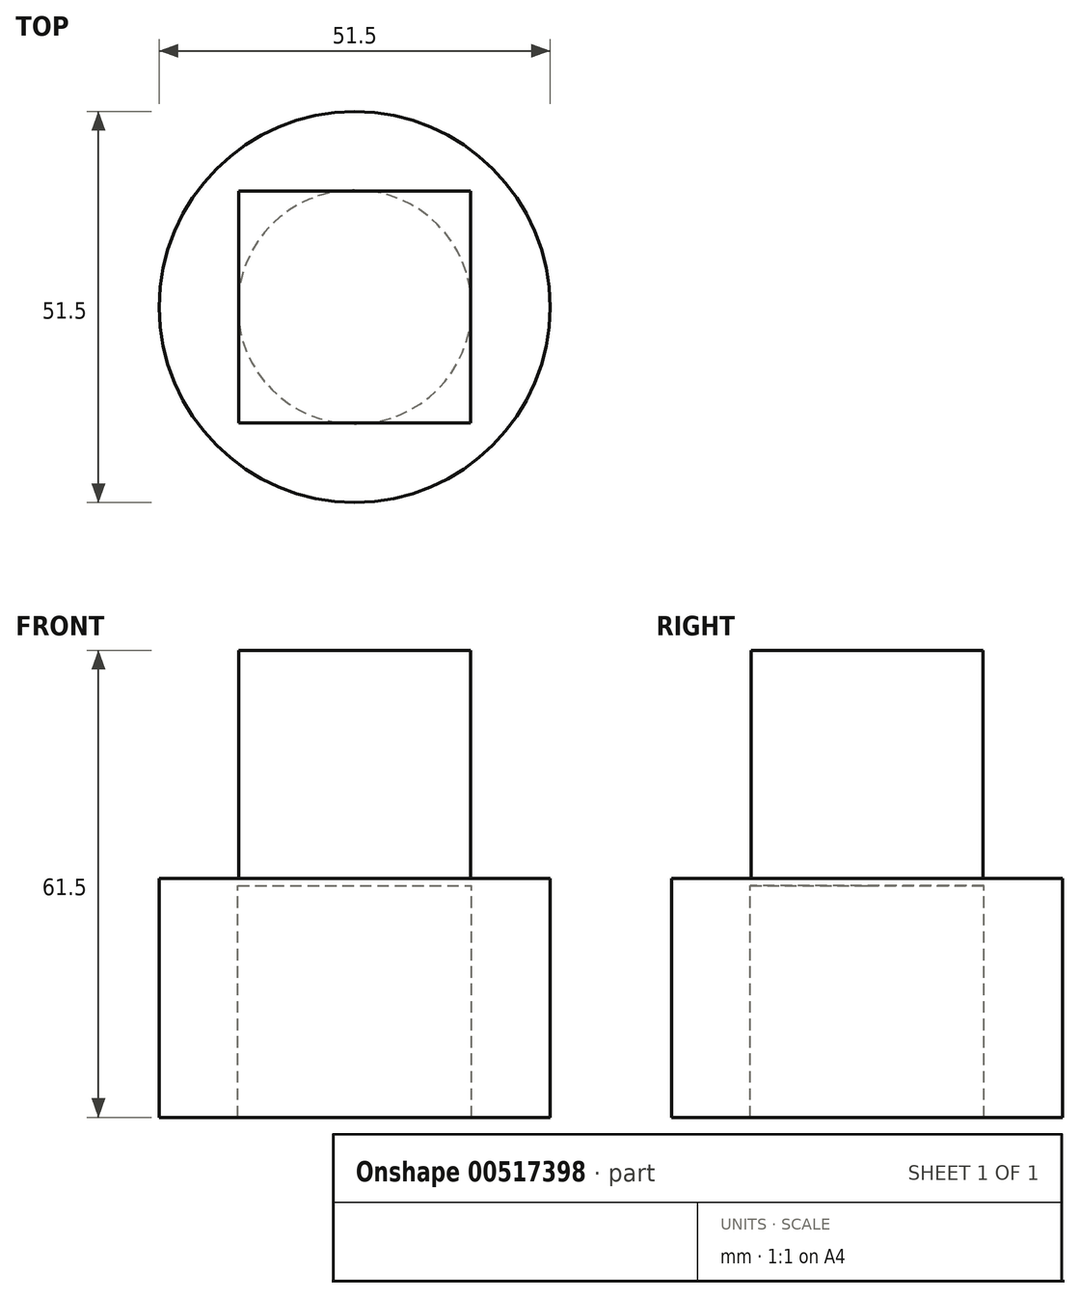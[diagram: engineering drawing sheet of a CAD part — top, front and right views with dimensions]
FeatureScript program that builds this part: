
annotation { "Feature Type Name" : "Feature", "Feature Type Description" : "" }
export const myFeature = defineFeature(function(context is Context, id is Id, definition is map)
    precondition{}
    {
        {
            var Q0;
            Q0=qCreatedBy(makeId("Top.planeOp"),FACE);
            var sketch = newSketch(context, id + "F0", { "sketchPlane" : qUnion([Q0])});
            skLineSegment(sketch, "E0.bottom", {"start": v(15.25, 15.25) * mm, "end": v(-15.25, 15.25) * mm});
            skLineSegment(sketch, "E0.top", {"start": v(15.25, -15.25) * mm, "end": v(-15.25, -15.25) * mm});
            skLineSegment(sketch, "E0.left", {"start": v(15.25, 15.25) * mm, "end": v(15.25, -15.25) * mm});
            skLineSegment(sketch, "E0.right", {"start": v(-15.25, 15.25) * mm, "end": v(-15.25, -15.25) * mm});
            skPoint(sketch, "E0.middle", {"position": v(0, 0) * mm});
            skSolve(sketch);
        }
        {
            var Q0;
            Q0=makeQuery(id+"F0.imprint","IMPRINT",FACE,{"disambiguationData":[TD([[makeQuery(id+"F0.imprint","IMPRINT",EDGE,{"derivedFrom":sQuery(id+"F0.wireOp",EDGE,"E0.bottom")}),1.0]])]});
            extrude(context, id + "F1", {"entities" : qUnion([Q0]), "depth" : 30 * mm, "offsetDistance" : 25 * mm});
        }
        {
            var Q0;
            Q0=makeQuery(id+"F1.opExtrude","CAP_FACE",FACE,{"disambiguationData":[OSD([sQuery(id+"F0.wireOp",EDGE,"E0.bottom"),sQuery(id+"F0.wireOp",EDGE,"E0.top"),sQuery(id+"F0.wireOp",EDGE,"E0.left"),sQuery(id+"F0.wireOp",EDGE,"E0.right")])],"isStart":true});
            var sketch = newSketch(context, id + "F2", { "sketchPlane" : qUnion([Q0])});
            skCircle(sketch, "E1", {"center": v(0, 0) * mm, "radius": 25.75 * mm});
            skCircle(sketch, "E2", {"center": v(0, 0) * mm, "radius": 15 * mm});
            skSolve(sketch);
        }
        {
            var Q0;
            Q0=makeQuery(id+"F2.imprint","IMPRINT",FACE,{"disambiguationData":[TD([[makeQuery(id+"F2.imprint","IMPRINT",EDGE,{"derivedFrom":sQuery(id+"F2.wireOp",EDGE,"E1")}),1.0]])]});
            var Q1;
            {var subQ0=sQuery(id+"F2.wireOp",EDGE,"E2");var subQ1=makeQuery(id+"F2.imprint","INTERSECT",VERTEX,{"derivedFrom":[makeQuery(id+"F1.opExtrude","CAP_EDGE",EDGE,{"disambiguationData":[OSD([sQuery(id+"F0.wireOp",EDGE,"E0.top")])],"isStart":true}),subQ0]});Q1=makeQuery(id+"F2.imprint","IMPRINT",FACE,{"disambiguationData":[TD([[makeQuery(id+"F2.imprint","IMPRINT",EDGE,{"disambiguationData":[TD([[subQ1,1.0]])],"derivedFrom":subQ0}),1.0]])]});}
            var Q2;
            {var subQ0=sQuery(id+"F2.wireOp",EDGE,"E2");var subQ1=makeQuery(id+"F1.opExtrude","CAP_EDGE",EDGE,{"disambiguationData":[OSD([sQuery(id+"F0.wireOp",EDGE,"E0.top")])],"isStart":true});var subQ2=makeQuery(id+"F2.imprint","INTERSECT",VERTEX,{"derivedFrom":[subQ1,subQ0]});Q2=makeQuery(id+"F2.imprint","IMPRINT",FACE,{"disambiguationData":[TD([[makeQuery(id+"F2.imprint","IMPRINT",EDGE,{"disambiguationData":[TD([[subQ2,-1.0]])],"derivedFrom":subQ0}),-1.0]])]});}
            var Q3;
            {var subQ0=sQuery(id+"F2.wireOp",EDGE,"E2");var subQ1=makeQuery(id+"F1.opExtrude","CAP_EDGE",EDGE,{"disambiguationData":[OSD([sQuery(id+"F0.wireOp",EDGE,"E0.top")])],"isStart":true});var subQ2=makeQuery(id+"F2.imprint","INTERSECT",VERTEX,{"derivedFrom":[subQ1,subQ0]});Q3=makeQuery(id+"F2.imprint","IMPRINT",FACE,{"disambiguationData":[TD([[makeQuery(id+"F2.imprint","IMPRINT",EDGE,{"disambiguationData":[TD([[subQ2,1.0]])],"derivedFrom":subQ0}),-1.0]])]});}
            var Q4;
            {var subQ0=sQuery(id+"F2.wireOp",EDGE,"E2");var subQ1=makeQuery(id+"F1.opExtrude","CAP_EDGE",EDGE,{"disambiguationData":[OSD([sQuery(id+"F0.wireOp",EDGE,"E0.left")])],"isStart":true});var subQ2=makeQuery(id+"F2.imprint","INTERSECT",VERTEX,{"derivedFrom":[subQ1,subQ0]});Q4=makeQuery(id+"F2.imprint","IMPRINT",FACE,{"disambiguationData":[TD([[makeQuery(id+"F2.imprint","IMPRINT",EDGE,{"disambiguationData":[TD([[subQ2,1.0]])],"derivedFrom":subQ0}),-1.0]])]});}
            var Q5;
            {var subQ0=sQuery(id+"F2.wireOp",EDGE,"E2");var subQ1=makeQuery(id+"F1.opExtrude","CAP_EDGE",EDGE,{"disambiguationData":[OSD([sQuery(id+"F0.wireOp",EDGE,"E0.right")])],"isStart":true});var subQ2=makeQuery(id+"F2.imprint","INTERSECT",VERTEX,{"derivedFrom":[subQ1,subQ0]});Q5=makeQuery(id+"F2.imprint","IMPRINT",FACE,{"disambiguationData":[TD([[makeQuery(id+"F2.imprint","IMPRINT",EDGE,{"disambiguationData":[TD([[subQ2,-1.0]])],"derivedFrom":subQ0}),-1.0]])]});}
            extrude(context, id + "F3", {"entities" : qUnion([Q0, Q1, Q2, Q3, Q4, Q5]), "operationType" : NewBodyOperationType.ADD, "depth" : 1 * mm, "offsetDistance" : 25 * mm});
        }
        {
            var Q0;
            Q0=makeQuery(id+"F3.opExtrude","CAP_FACE",FACE,{"disambiguationData":[OSD([sQuery(id+"F2.wireOp",EDGE,"E1")])],"isStart":false});
            var sketch = newSketch(context, id + "F4", { "sketchPlane" : qUnion([Q0])});
            skCircle(sketch, "E3.0", {"center": v(0, 0) * mm, "radius": 15 * mm, "construction": true});
            skCircle(sketch, "E4.0", {"center": v(0, 0) * mm, "radius": 25.75 * mm});
            skCircle(sketch, "E5.0", {"center": v(0, 0) * mm, "radius": 15.4 * mm});
            skSolve(sketch);
        }
        {
            var Q0;
            Q0=makeQuery(id+"F4.imprint","IMPRINT",FACE,{"disambiguationData":[TD([[makeQuery(id+"F4.imprint","IMPRINT",EDGE,{"derivedFrom":sQuery(id+"F4.wireOp",EDGE,"E3.0")}),-1.0]])]});
            var Q1;
            Q1=makeQuery(id+"F4.imprint","IMPRINT",FACE,{"disambiguationData":[TD([[makeQuery(id+"F4.imprint","IMPRINT",EDGE,{"derivedFrom":sQuery(id+"F4.wireOp",EDGE,"E4.0")}),1.0]])]});
            extrude(context, id + "F5", {"entities" : qUnion([Q0, Q1]), "operationType" : NewBodyOperationType.ADD, "depth" : 30.5 * mm, "offsetDistance" : 25 * mm});
        }
    });
